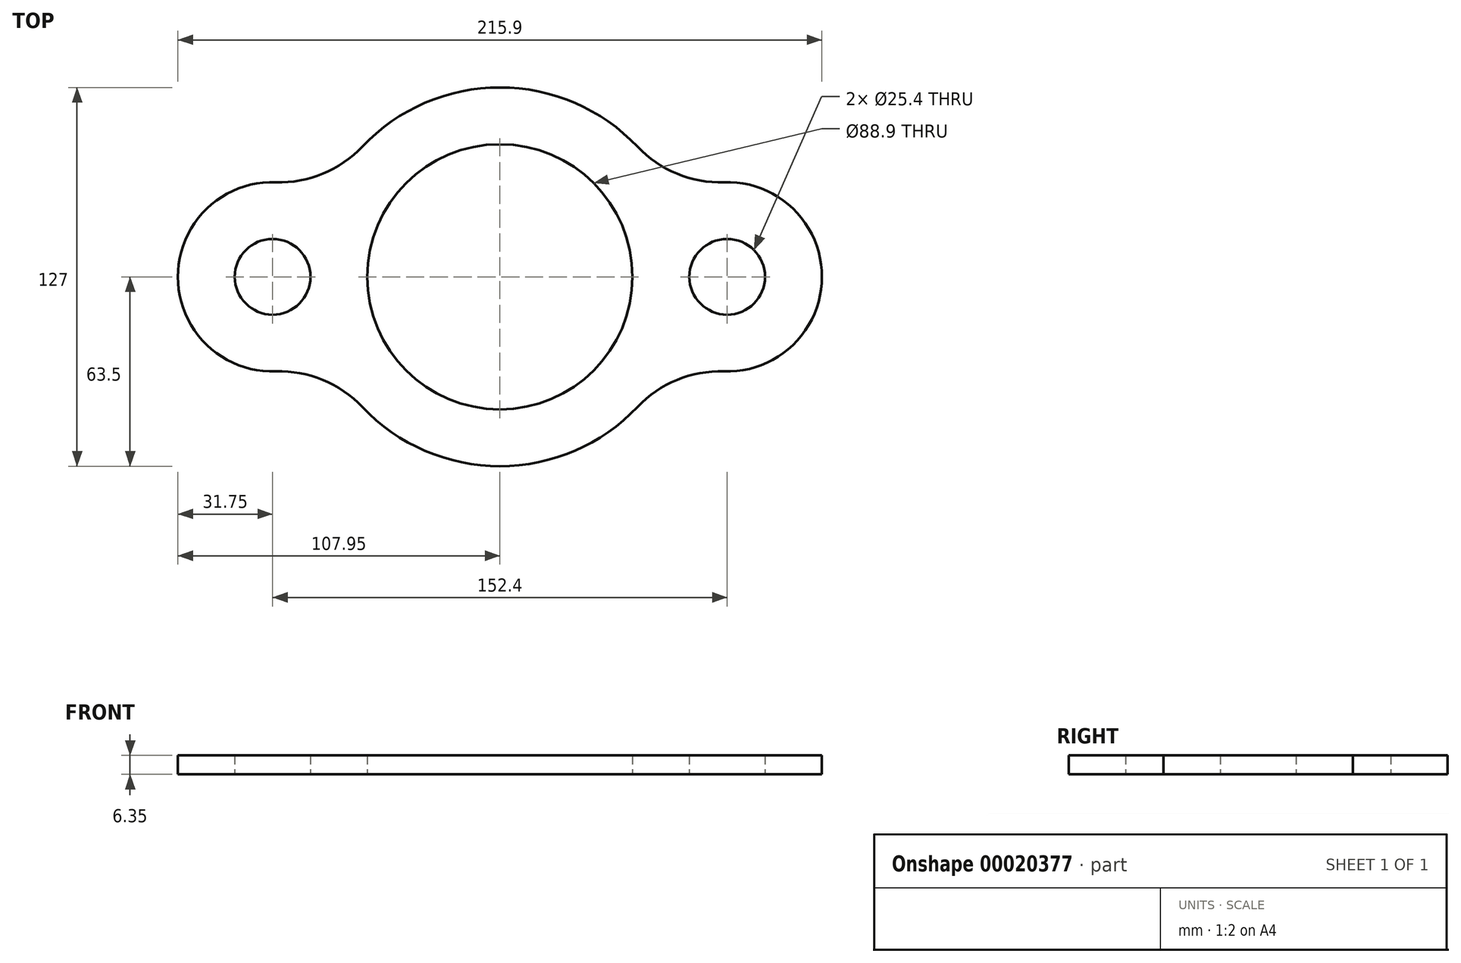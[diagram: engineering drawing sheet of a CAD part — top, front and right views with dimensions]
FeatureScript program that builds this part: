
annotation { "Feature Type Name" : "Feature", "Feature Type Description" : "" }
export const myFeature = defineFeature(function(context is Context, id is Id, definition is map)
    precondition{}
    {
        {
            var Q0;
            Q0=qCreatedBy(makeId("Top.planeOp"),FACE);
            var sketch = newSketch(context, id + "F0", { "sketchPlane" : qUnion([Q0])});
            skCircle(sketch, "E0", {"center": v(0, 0) * mm, "radius": 44.45 * mm});
            skArc(sketch, "E1", {"start": v(46.14, 43.63) * mm, "mid": v(0, 63.5) * mm, "end": v(-46.14, 43.63) * mm});
            skLineSegment(sketch, "E2", {"start": v(63.5, 0) * mm, "end": v(76.2, 0) * mm});
            skCircle(sketch, "E3", {"center": v(76.2, 0) * mm, "radius": 12.7 * mm});
            skArc(sketch, "E4", {"start": v(75.12, -31.73) * mm, "mid": v(107.95, 0) * mm, "end": v(75.12, 31.73) * mm});
            skLineSegment(sketch, "E5", {"start": v(-63.5, 0) * mm, "end": v(-76.2, 0) * mm});
            skCircle(sketch, "E6", {"center": v(-76.2, 0) * mm, "radius": 12.7 * mm});
            skArc(sketch, "E7", {"start": v(-75.12, 31.73) * mm, "mid": v(-107.95, 0) * mm, "end": v(-75.12, -31.73) * mm});
            skArc(sketch, "E8.trimOffspring", {"start": v(-46.14, -43.63) * mm, "mid": v(0, -63.5) * mm, "end": v(46.14, -43.63) * mm});
            skPoint(sketch, "E9.visualSharp", {"position": v(57.94, 25.98) * mm});
            skArc(sketch, "E9.filletArc", {"start": v(46.14, 43.63) * mm, "mid": v(59.35, 34.56) * mm, "end": v(75.12, 31.73) * mm});
            skPoint(sketch, "E10.visualSharp", {"position": v(-57.94, 25.98) * mm});
            skArc(sketch, "E10.filletArc", {"start": v(-75.12, 31.73) * mm, "mid": v(-59.35, 34.56) * mm, "end": v(-46.14, 43.63) * mm});
            skPoint(sketch, "E11.visualSharp", {"position": v(-57.94, -25.98) * mm});
            skArc(sketch, "E11.filletArc", {"start": v(-46.14, -43.63) * mm, "mid": v(-59.35, -34.56) * mm, "end": v(-75.12, -31.73) * mm});
            skPoint(sketch, "E12.visualSharp", {"position": v(57.94, -25.98) * mm});
            skArc(sketch, "E12.filletArc", {"start": v(75.12, -31.73) * mm, "mid": v(59.35, -34.56) * mm, "end": v(46.14, -43.63) * mm});
            skSolve(sketch);
        }
        {
            var Q0;
            Q0=makeQuery(id+"F0.imprint","IMPRINT",FACE,{"disambiguationData":[TD([[makeQuery(id+"F0.imprint","IMPRINT",EDGE,{"derivedFrom":sQuery(id+"F0.wireOp",EDGE,"E0")}),-1.0]])]});
            extrude(context, id + "F1", {"entities" : qUnion([Q0]), "depth" : 6.35 * mm});
        }
    });
